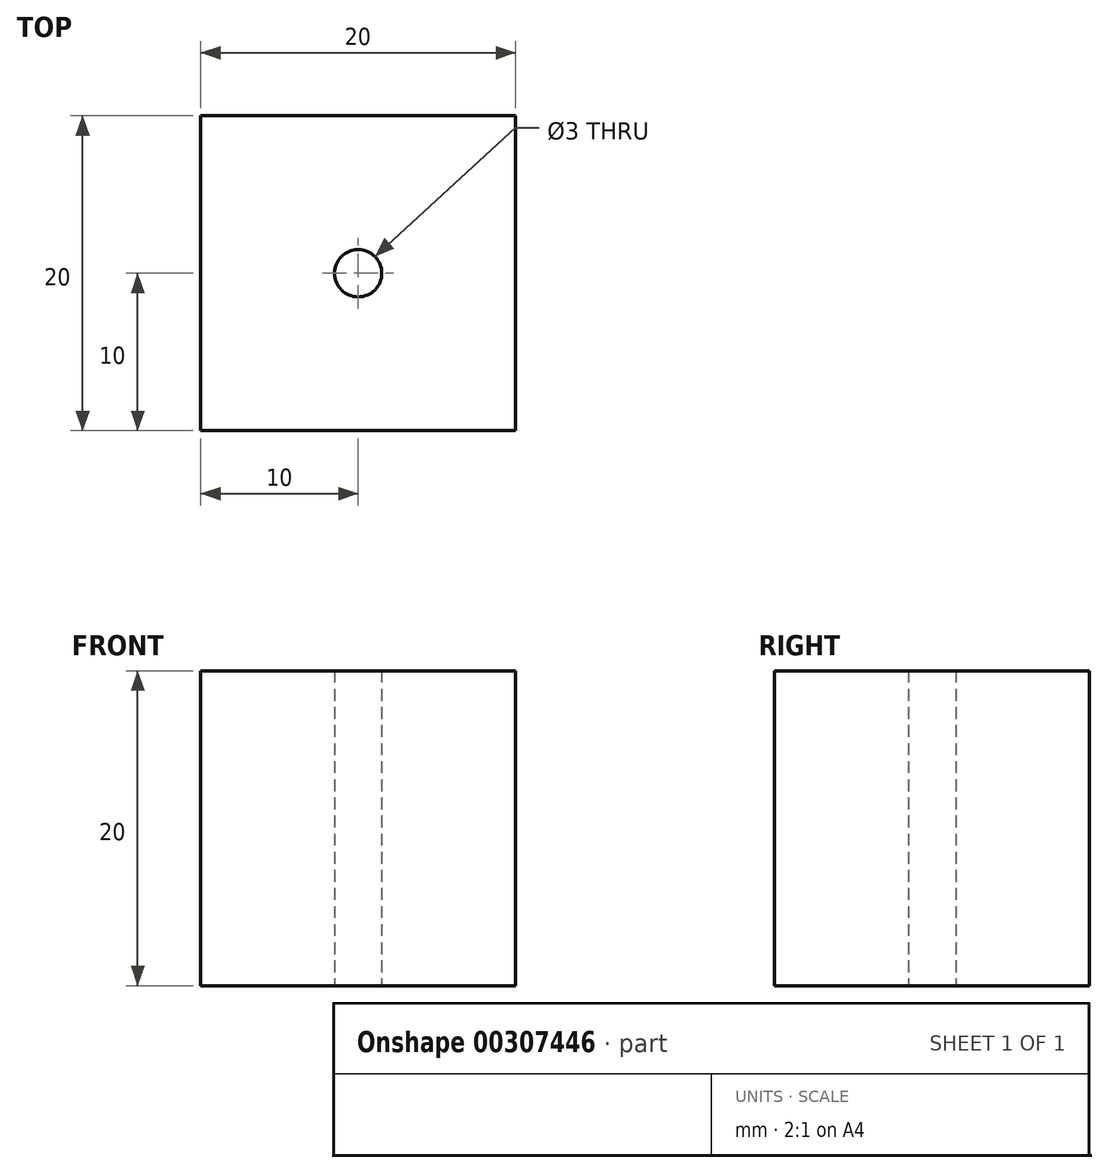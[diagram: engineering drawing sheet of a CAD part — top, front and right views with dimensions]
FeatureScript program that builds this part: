
annotation { "Feature Type Name" : "Feature", "Feature Type Description" : "" }
export const myFeature = defineFeature(function(context is Context, id is Id, definition is map)
    precondition{}
    {
        {
            var Q0;
            Q0=qCreatedBy(makeId("Top.planeOp"),FACE);
            var sketch = newSketch(context, id + "F0", { "sketchPlane" : qUnion([Q0])});
            skLineSegment(sketch, "E0.bottom", {"start": v(0, 0) * mm, "end": v(20, 0) * mm});
            skLineSegment(sketch, "E0.top", {"start": v(0, 20) * mm, "end": v(20, 20) * mm});
            skLineSegment(sketch, "E0.left", {"start": v(0, 0) * mm, "end": v(0, 20) * mm});
            skLineSegment(sketch, "E0.right", {"start": v(20, 0) * mm, "end": v(20, 20) * mm});
            skLineSegment(sketch, "E1", {"start": v(10, 0) * mm, "end": v(10, 20) * mm, "construction": true});
            skCircle(sketch, "E2", {"center": v(10, 10) * mm, "radius": 1.5 * mm});
            skSolve(sketch);
        }
        {
            var Q0;
            Q0=makeQuery(id+"F0.imprint","IMPRINT",FACE,{"disambiguationData":[TD([[makeQuery(id+"F0.imprint","IMPRINT",EDGE,{"derivedFrom":sQuery(id+"F0.wireOp",EDGE,"E0.bottom")}),1.0]])]});
            extrude(context, id + "F1", {"entities" : qUnion([Q0]), "depth" : 20 * mm});
        }
    });
